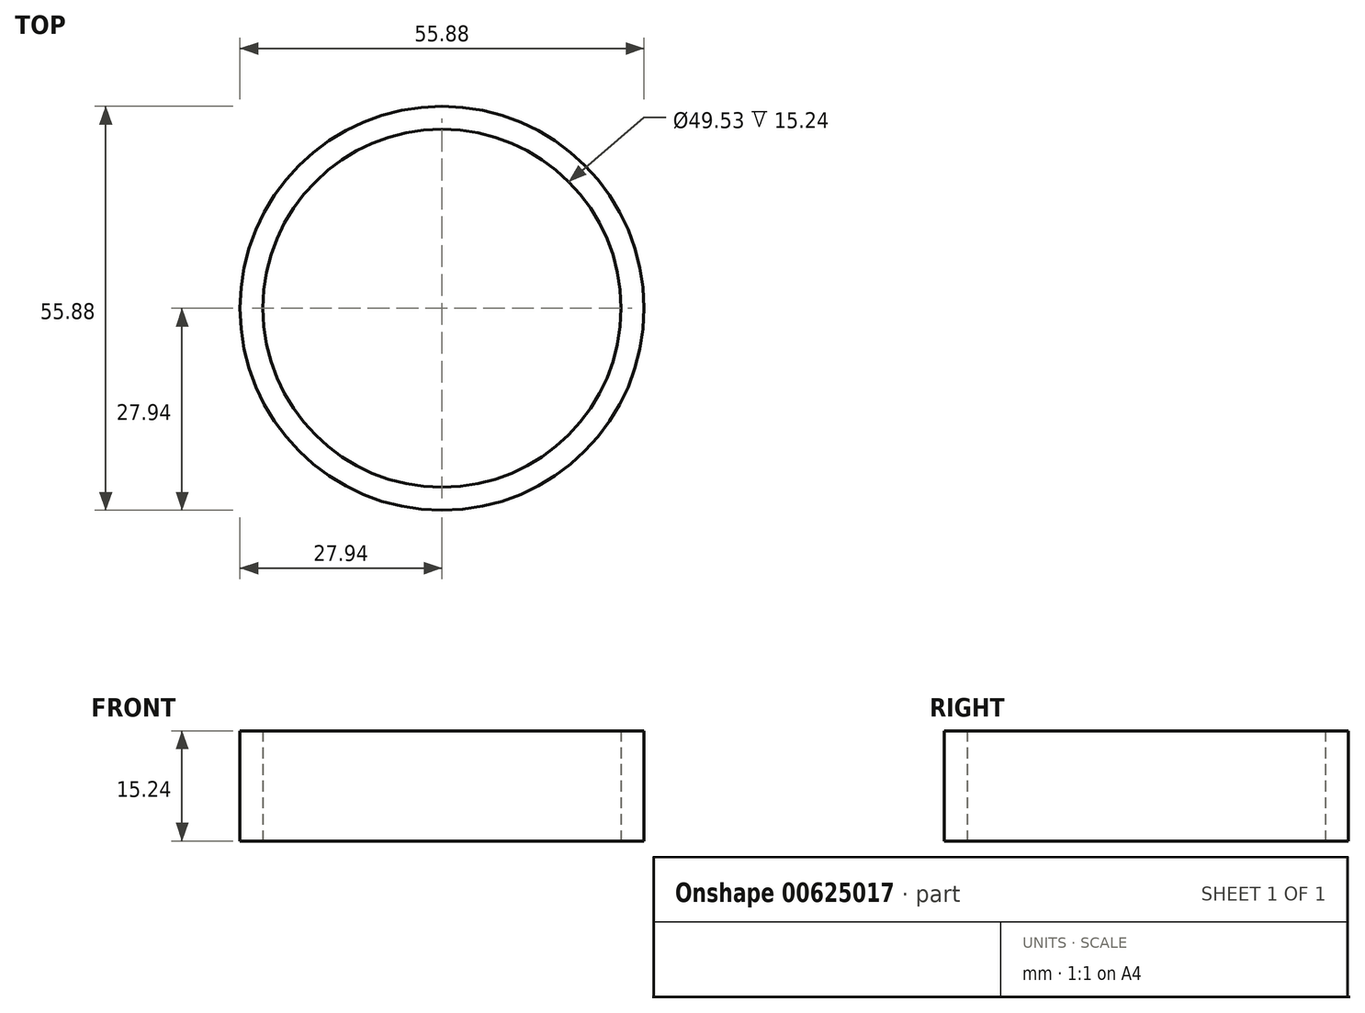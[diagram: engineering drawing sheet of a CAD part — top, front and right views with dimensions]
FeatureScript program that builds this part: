
annotation { "Feature Type Name" : "Feature", "Feature Type Description" : "" }
export const myFeature = defineFeature(function(context is Context, id is Id, definition is map)
    precondition{}
    {
        {
            var Q0;
            Q0=qCreatedBy(makeId("Top.planeOp"),FACE);
            var sketch = newSketch(context, id + "F0", { "sketchPlane" : qUnion([Q0])});
            skCircle(sketch, "E0", {"center": v(0, 0) * mm, "radius": 24.77 * mm});
            skCircle(sketch, "E1", {"center": v(0, 0) * mm, "radius": 27.94 * mm});
            skSolve(sketch);
        }
        {
            var Q0;
            Q0=makeQuery(id+"F0.imprint","IMPRINT",FACE,{"disambiguationData":[TD([[makeQuery(id+"F0.imprint","IMPRINT",EDGE,{"derivedFrom":sQuery(id+"F0.wireOp",EDGE,"E0")}),-1.0]])]});
            extrude(context, id + "F1", {"entities" : qUnion([Q0]), "depth" : 15.24 * mm, "offsetDistance" : 25.4 * mm});
        }
    });
